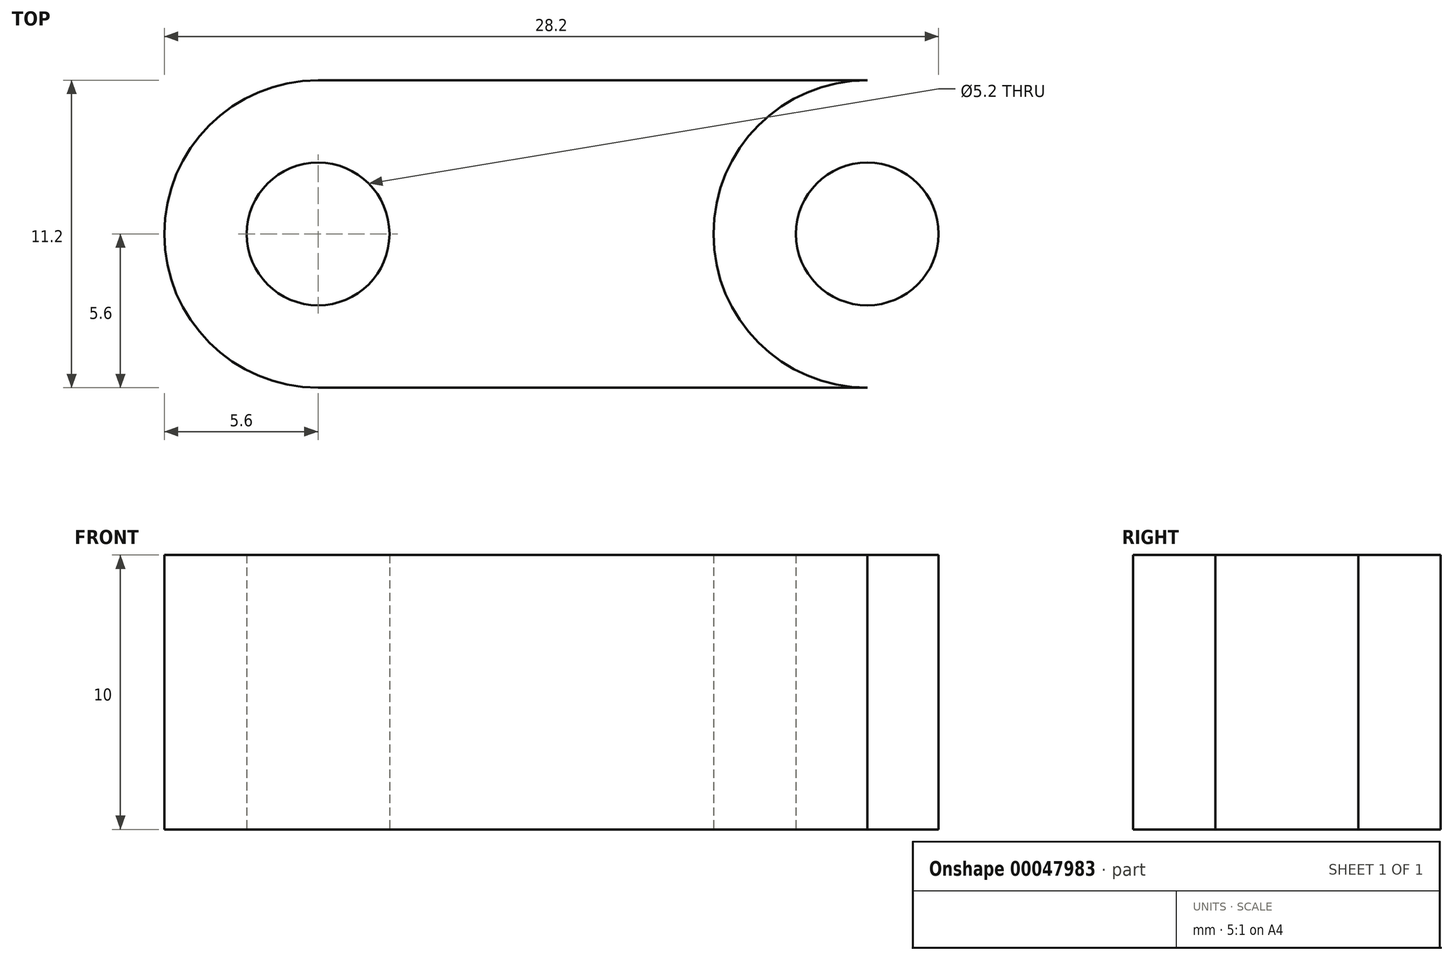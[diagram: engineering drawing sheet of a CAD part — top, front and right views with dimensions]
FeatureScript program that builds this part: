
annotation { "Feature Type Name" : "Feature", "Feature Type Description" : "" }
export const myFeature = defineFeature(function(context is Context, id is Id, definition is map)
    precondition{}
    {
        {
            assignVariable(context, id + "F0", {"name" : "spacerHeight", "anyValue" : 10});
        }
        {
            var Q0;
            Q0=qCreatedBy(makeId("Top.planeOp"),FACE);
            var sketch = newSketch(context, id + "F1", { "sketchPlane" : qUnion([Q0])});
            skCircle(sketch, "E0", {"center": v(-10, 0) * mm, "radius": 5.6 * mm});
            skLineSegment(sketch, "E1", {"start": v(-10, 0) * mm, "end": v(-10, 5.6) * mm});
            skLineSegment(sketch, "E2", {"start": v(-10, 5.6) * mm, "end": v(0, 5.6) * mm});
            skLineSegment(sketch, "E3", {"start": v(-10, 0) * mm, "end": v(-10, -5.6) * mm});
            skLineSegment(sketch, "E4", {"start": v(-10, -5.6) * mm, "end": v(0, -5.6) * mm});
            skLineSegment(sketch, "E5", {"start": v(0, -5.6) * mm, "end": v(0, 0) * mm});
            skLineSegment(sketch, "E6", {"start": v(0, 0) * mm, "end": v(0, 5.6) * mm});
            skCircle(sketch, "E7", {"center": v(-10, 0) * mm, "radius": 2.6 * mm});
            skLineSegment(sketch, "E8.MirrorCS", {"start": v(10, 5.6) * mm, "end": v(0, 5.6) * mm});
            skLineSegment(sketch, "E9.MirrorCS", {"start": v(10, -5.6) * mm, "end": v(0, -5.6) * mm});
            skCircle(sketch, "E10.MirrorC", {"center": v(10, 0) * mm, "radius": 5.6 * mm});
            skCircle(sketch, "E11.MirrorC", {"center": v(10, 0) * mm, "radius": 2.6 * mm});
            skSolve(sketch);
        }
        {
            var Q0;
            {var subQ0=sQuery(id+"F1.wireOp",EDGE,"E7");var subQ3=sQuery(id+"F1.wireOp",EDGE,"E1");var subQ4=makeQuery(id+"F1.imprint","INTERSECT",VERTEX,{"derivedFrom":[subQ3,subQ0]});Q0=makeQuery(id+"F1.imprint","IMPRINT",FACE,{"disambiguationData":[TD([[makeQuery(id+"F1.imprint","IMPRINT",EDGE,{"disambiguationData":[TD([[subQ4,1.0]])],"derivedFrom":subQ0}),-1.0]])]});}
            var Q1;
            {var subQ0=sQuery(id+"F1.wireOp",EDGE,"E7");var subQ3=sQuery(id+"F1.wireOp",EDGE,"E1");var subQ4=makeQuery(id+"F1.imprint","INTERSECT",VERTEX,{"derivedFrom":[subQ3,subQ0]});Q1=makeQuery(id+"F1.imprint","IMPRINT",FACE,{"disambiguationData":[TD([[makeQuery(id+"F1.imprint","IMPRINT",EDGE,{"disambiguationData":[TD([[subQ4,-1.0]])],"derivedFrom":subQ0}),-1.0]])]});}
            var Q2;
            {var subQ0=sQuery(id+"F1.wireOp",EDGE,"E2");Q2=makeQuery(id+"F1.imprint","IMPRINT",FACE,{"disambiguationData":[TD([[makeQuery(id+"F1.imprint","IMPRINT",EDGE,{"derivedFrom":subQ0}),-1.0]])]});}
            var Q3;
            Q3=makeQuery(id+"F1.imprint","IMPRINT",FACE,{"disambiguationData":[TD([[makeQuery(id+"F1.imprint","IMPRINT",EDGE,{"derivedFrom":sQuery(id+"F1.wireOp",EDGE,"E5")}),-1.0]])]});
            var Q4;
            Q4=makeQuery(id+"F1.imprint","IMPRINT",FACE,{"disambiguationData":[TD([[makeQuery(id+"F1.imprint","IMPRINT",EDGE,{"derivedFrom":sQuery(id+"F1.wireOp",EDGE,"E11.MirrorC")}),1.0]])]});
            extrude(context, id + "F2", {"entities" : qUnion([Q0, Q1, Q2, Q3, Q4]), "depth" : (getVariable(context, 'spacerHeight')) * mm});
        }
    });
